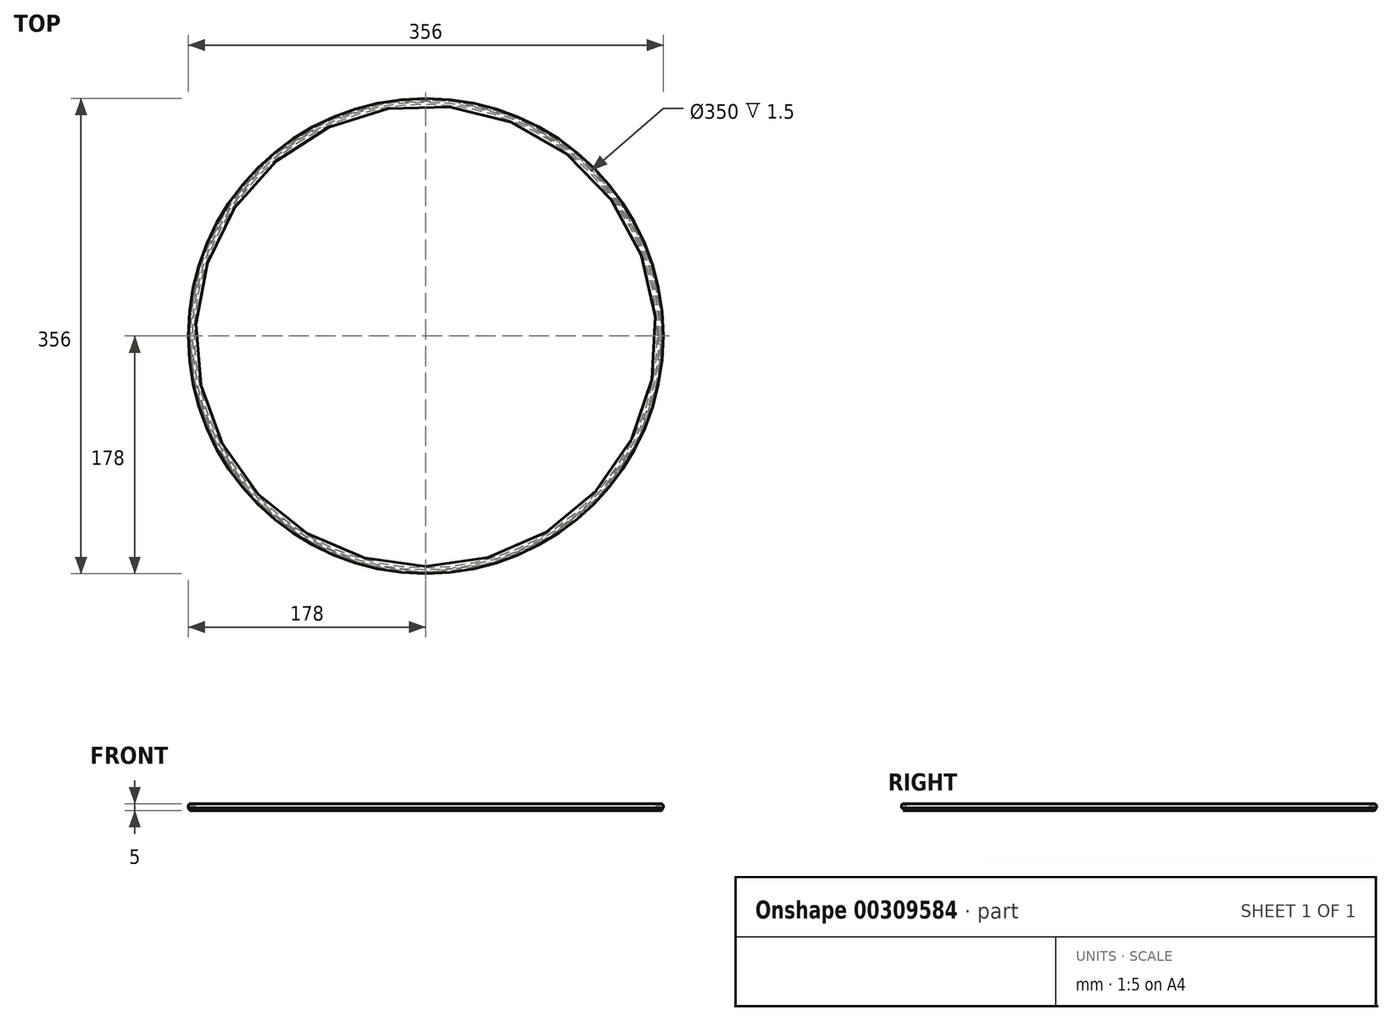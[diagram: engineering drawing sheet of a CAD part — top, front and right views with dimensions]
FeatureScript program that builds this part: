
annotation { "Feature Type Name" : "Feature", "Feature Type Description" : "" }
export const myFeature = defineFeature(function(context is Context, id is Id, definition is map)
    precondition{}
    {
        {
            var Q0;
            Q0=qCreatedBy(makeId("Top.planeOp"),FACE);
            var sketch = newSketch(context, id + "F0", { "sketchPlane" : qUnion([Q0])});
            skCircle(sketch, "E0", {"center": v(0, 0) * mm, "radius": 175 * mm});
            skSolve(sketch);
        }
        {
            var Q0;
            Q0=qCreatedBy(makeId("Right.planeOp"),FACE);
            var sketch = newSketch(context, id + "F1", { "sketchPlane" : qUnion([Q0])});
            skLineSegment(sketch, "E1.0", {"start": v(-175, 0) * mm, "end": v(175, 0) * mm});
            skCircle(sketch, "E2", {"center": v(-175, 0) * mm, "radius": 2.5 * mm});
            skLineSegment(sketch, "E3", {"start": v(-176.5, -2) * mm, "end": v(-173.5, -2) * mm});
            skSolve(sketch);
        }
        {
            var Q0;
            {var subQ0=sQuery(id+"F1.wireOp",EDGE,"E3");Q0=makeQuery(id+"F1.imprint","IMPRINT",FACE,{"disambiguationData":[TD([[makeQuery(id+"F1.imprint","IMPRINT",EDGE,{"derivedFrom":subQ0}),1.0]])]});}
            var Q1;
            Q1=sQuery(id+"F0.wireOp",EDGE,"E0");
            sweep(context, id + "F2", {"profiles" : qUnion([Q0]), "path" : qUnion([Q1])});
        }
        {
            var Q0;
            Q0=qCreatedBy(makeId("Front.planeOp"),FACE);
            var sketch = newSketch(context, id + "F3", { "sketchPlane" : qUnion([Q0])});
            skLineSegment(sketch, "E4.bottom", {"start": v(175, 0) * mm, "end": v(178, 0) * mm});
            skLineSegment(sketch, "E4.top", {"start": v(175, 3) * mm, "end": v(178, 3) * mm});
            skLineSegment(sketch, "E4.left", {"start": v(175, 0) * mm, "end": v(175, 3) * mm});
            skLineSegment(sketch, "E4.right", {"start": v(178, 0) * mm, "end": v(178, 3) * mm});
            skLineSegment(sketch, "E5", {"start": v(0, 0) * mm, "end": v(0, 38.17) * mm, "construction": true});
            skSolve(sketch);
        }
        {
            var Q0;
            Q0 = qSketchRegion(id + "F3", true);
            var Q1;
            Q1 = qConstructionFilter(qBodyType(qCreatedBy(id + "F3" ,EDGE), BodyType.WIRE), ConstructionObject.NO);
            var Q2;
            Q2=sQuery(id+"F3.wireOp",EDGE,"E5");
            revolve(context, id + "F4", {"surfaceOperationType" : NewSurfaceOperationType.NEW, "entities" : qUnion([Q0]), "surfaceEntities" : qUnion([Q1]), "axis" : qUnion([Q2]), "revolveType" : RevolveType.FULL});
        }
        {
            var Q0;
            Q0=makeQuery(id+"F4.opRevolve","SWEPT_EDGE",EDGE,{"disambiguationData":[OSD([sQuery(id+"F3.wireOp",EDGE,"E4.top"),sQuery(id+"F3.wireOp",EDGE,"E4.right")])]});
            var Q1;
            Q1=makeQuery(id+"F4.opRevolve","SWEPT_EDGE",EDGE,{"disambiguationData":[OSD([sQuery(id+"F3.wireOp",EDGE,"E4.top"),sQuery(id+"F3.wireOp",EDGE,"E4.left")])]});
            fillet(context, id + "F5", {"entities" : qUnion([Q0, Q1]), "radius" : 1.5 * mm, "tangentPropagation" : true, "allowEdgeOverflow" : false});
        }
    });
